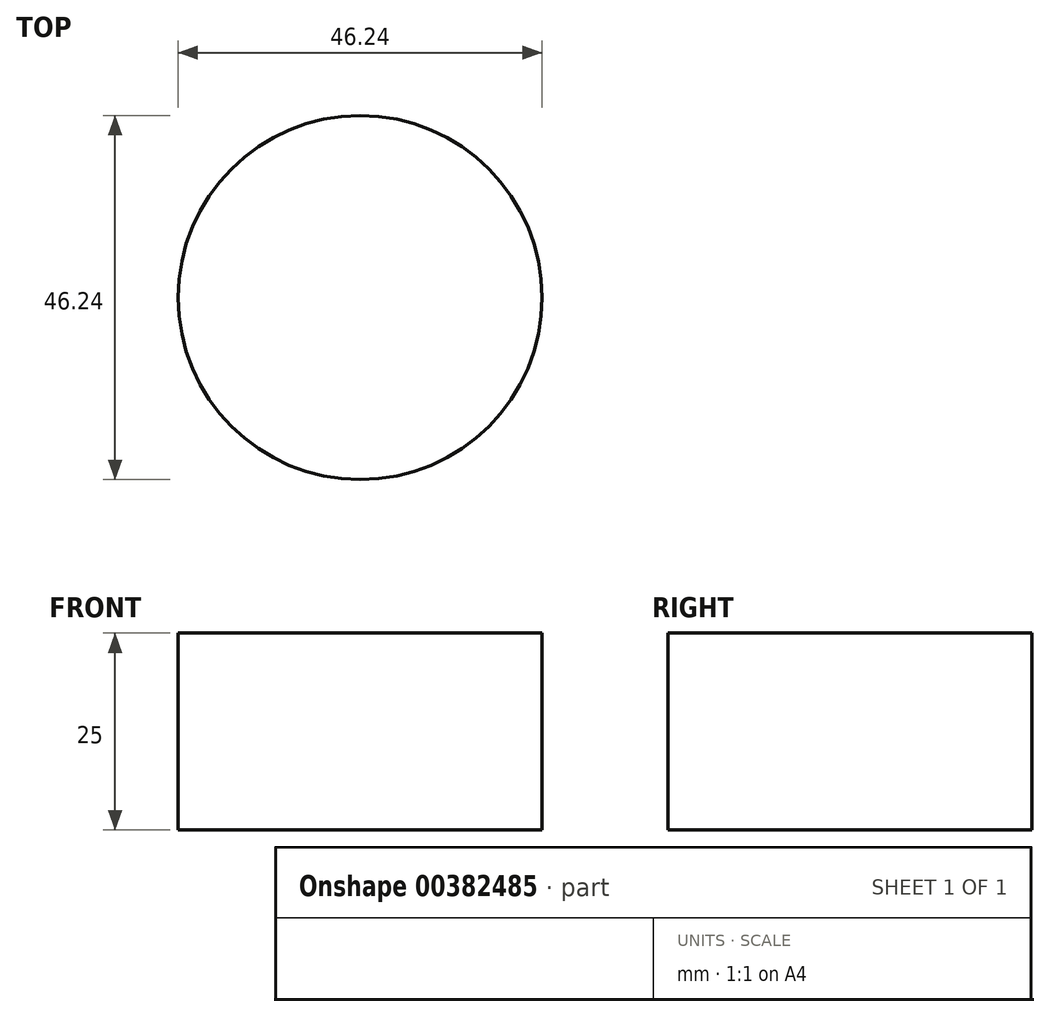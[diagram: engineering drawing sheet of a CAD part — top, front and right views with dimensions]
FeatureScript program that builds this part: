
annotation { "Feature Type Name" : "Feature", "Feature Type Description" : "" }
export const myFeature = defineFeature(function(context is Context, id is Id, definition is map)
    precondition{}
    {
        {
            var Q0;
            Q0=qCreatedBy(makeId("Top.planeOp"),FACE);
            var sketch = newSketch(context, id + "F0", { "sketchPlane" : qUnion([Q0])});
            skCircle(sketch, "E0", {"center": v(0, 0) * mm, "radius": 23.12 * mm});
            skSolve(sketch);
        }
        {
            var Q0;
            Q0 = qSketchRegion(id + "F0", true);
            extrude(context, id + "F1", {"entities" : qUnion([Q0]), "depth" : 25 * mm});
        }
    });
